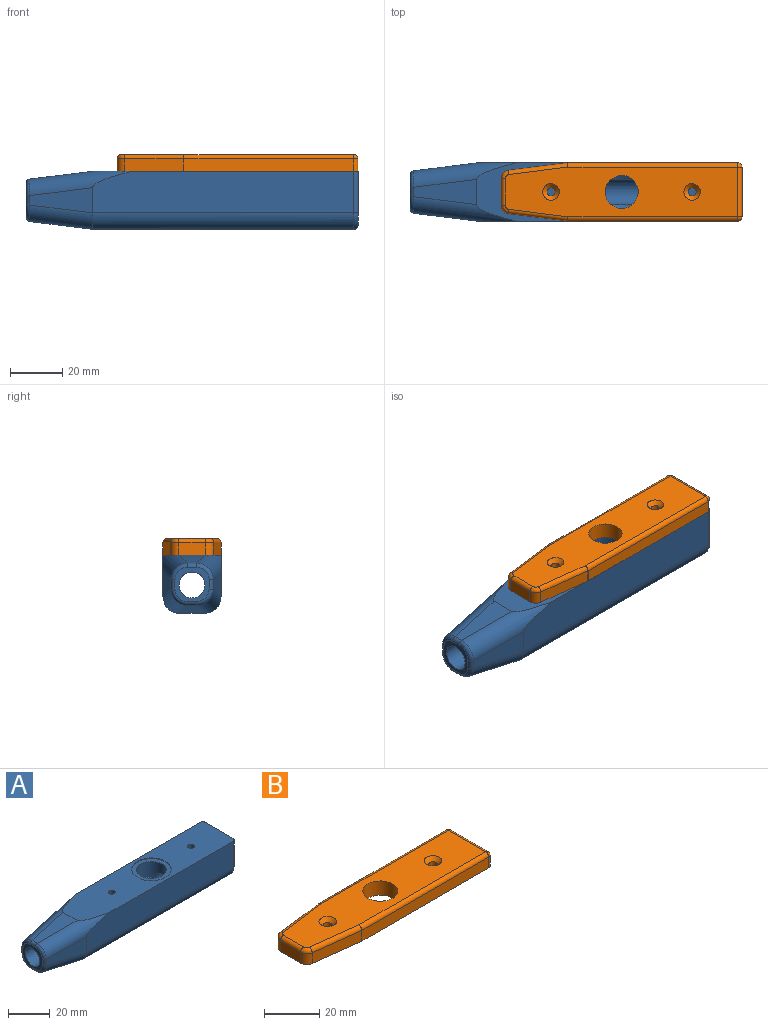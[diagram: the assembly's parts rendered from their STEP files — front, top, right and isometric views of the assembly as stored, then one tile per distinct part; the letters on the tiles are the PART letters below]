
ASSEMBLY  parts=2 mates=1
PART A: 39 faces, bbox 127x26x24.6 mm
  f0: plane 20.62x19.02mm, normal (1,0,0), area 305.2mm2, adj f2,f3,f32,f33,f34,f36,f38
  f1: plane 13.05x13.05mm, normal (-1,0,0), area 73.8mm2, adj f3,f20,f21,f22,f23,f25,f27,f29
  f2: plane 101.51x22.23mm, normal (0,0,1), area 1886mm2, adj f0,f4,f5,f11,f12,f14,f17,f28
  f3: cylinder r=4.97mm len=127mm, axis (1,0,0), area 3790.2mm2, adj f0,f1,f7,f8,f9
  f4: plane 99.91x15.88mm, normal (0,-1,0), area 1552mm2, adj f2,f16,f30,f34,f35
  f5: plane 99.91x15.88mm, normal (0,1,0), area 1552mm2, adj f2,f19,f28,f32,f37
  f6: plane 99.91x9.53mm, normal (0,0,-1), area 951.6mm2, adj f18,f33,f35,f37
  f7: cylinder r=7.15mm len=14.3mm, axis (0,0,1), area 366mm2, adj f3,f8,f9,f10
  f8: cone r=0mm half-angle=59deg, axis (0,0,1), area 19.5mm2, adj f3,f7
  f9: cone r=0mm half-angle=59deg, axis (0,0,1), area 19.5mm2, adj f3,f7
  f10: plane 19.05x19.05mm, normal (0,0,1), area 124.4mm2, adj f7,f11
  f11: cylinder r=9.53mm len=19.05mm, axis (0,0,1), area 24.3mm2, adj f2,f10
  f12: cylinder r=1.59mm len=3.18mm, axis (0,0,1), area 31.7mm2, adj f2,f13
  f13: plane 3.18x3.18mm, normal (0,0,1), area 7.9mm2, adj f12
  f14: cylinder r=1.59mm len=3.18mm, axis (0,0,1), area 31.7mm2, adj f2,f15
  f15: plane 3.18x3.18mm, normal (0,0,1), area 7.9mm2, adj f14
  f16: plane 24.09x9.62mm, normal (-0.12,-0.99,0), area 160.7mm2, adj f4,f20,f26,f30,f35
  f17: plane 24.09x9.62mm, normal (-0.12,0,0.99), area 160.7mm2, adj f2,f21,f28,f30
  f18: plane 24.09x9.62mm, normal (-0.12,0,-0.99), area 160.7mm2, adj f6,f22,f24,f26,f35,f37
  f19: plane 24.09x9.62mm, normal (-0.12,0.99,0), area 160.7mm2, adj f5,f23,f24,f28,f37
  f20: cylinder r=1.6mm len=3.62mm, axis (0,0,-1), area 8.4mm2, adj f1,f16,f27,f31
  f21: cylinder r=1.6mm len=3.62mm, axis (0,-1,0), area 8.4mm2, adj f1,f17,f29,f31
  f22: cylinder r=1.6mm len=3.62mm, axis (0,-1,0), area 8.4mm2, adj f1,f18,f25,f27
  f23: cylinder r=1.6mm len=3.62mm, axis (0,0,-1), area 8.4mm2, adj f1,f19,f25,f29
  f24: cylinder r=6.35mm len=24.4mm, axis (-0.98,-0.12,0.12), area 240mm2, adj f18,f19,f25,f37
  f25: bspline ~6.63x6.63mm, area 20.2mm2, adj f1,f22,f23,f24
  f26: cylinder r=6.35mm len=24.4mm, axis (0.98,-0.12,-0.12), area 240mm2, adj f16,f18,f27,f35
  f27: bspline ~6.3x6.3mm, area 20.2mm2, adj f1,f20,f22,f26
  f28: cylinder r=6.35mm len=39.49mm, axis (-0.98,-0.12,-0.12), area 292.5mm2, adj f2,f5,f17,f19,f29
  f29: bspline ~6.63x6.63mm, area 20.2mm2, adj f1,f21,f23,f28
  f30: cylinder r=6.35mm len=39.49mm, axis (0.98,-0.12,0.12), area 292.5mm2, adj f2,f4,f16,f17,f31
  f31: bspline ~6.3x6.3mm, area 20.2mm2, adj f1,f20,f21,f30
  f32: cylinder r=1.6mm len=15.88mm, axis (0,0,-1), area 39.9mm2, adj f0,f2,f5,f38
  f33: cylinder r=1.6mm len=9.53mm, axis (0,1,0), area 23.9mm2, adj f0,f6,f36,f38
  f34: cylinder r=1.6mm len=15.88mm, axis (0,0,1), area 39.9mm2, adj f0,f2,f4,f36
  f35: cylinder r=6.35mm len=100.07mm, axis (1,0,0), area 997.6mm2, adj f4,f6,f16,f18,f26,f36
  f36: torus R=4.75mm, axis (-1,0,0), area 22.8mm2, adj f0,f33,f34,f35
  f37: cylinder r=6.35mm len=100.07mm, axis (-1,0,0), area 997.6mm2, adj f5,f6,f18,f19,f24,f38
  f38: torus R=4.75mm, axis (-1,0,0), area 22.8mm2, adj f0,f32,f33,f37
PART B: 31 faces, bbox 92.1x22.2x6.4 mm
  f0: plane 64.98x4.75mm, normal (0,-1,0), area 308.6mm2, adj f5,f15,f18,f30
  f1: plane 19.02x4.75mm, normal (1,0,0), area 90.4mm2, adj f5,f16,f18,f20
  f2: plane 64.98x4.75mm, normal (0,1,0), area 308.6mm2, adj f5,f17,f20,f22
  f3: plane 10.27x4.75mm, normal (-1,0,0), area 48.8mm2, adj f5,f13,f14,f26
  f4: plane 88.87x19.02mm, normal (0,0,1), area 1428.6mm2, adj f6,f8,f10,f15,f16,f17,f24,f25
  f5: plane 92.08x22.23mm, normal (0,0,-1), area 1818.9mm2, adj f0,f1,f2,f3,f6,f7,f9,f11
  f6: cylinder r=6.35mm len=12.7mm, axis (0,0,-1), area 253.4mm2, adj f4,f5
  f7: cylinder r=1.59mm len=4.76mm, axis (0,0,1), area 47.5mm2, adj f5,f8
  f8: cone r=1.59mm half-angle=45deg, axis (0,0,1), area 33.6mm2, adj f4,f7
  f9: cylinder r=1.59mm len=4.76mm, axis (0,0,1), area 47.5mm2, adj f5,f10
  f10: cone r=1.59mm half-angle=45deg, axis (0,0,1), area 33.6mm2, adj f4,f9
  f11: plane 22.52x4.75mm, normal (-0.12,-0.99,0), area 107.8mm2, adj f5,f13,f28,f30
  f12: plane 22.52x4.75mm, normal (-0.12,0.99,0), area 107.8mm2, adj f5,f14,f22,f24
  f13: cylinder r=3.17mm len=4.75mm, axis (0,0,-1), area 21.8mm2, adj f3,f5,f11,f27
  f14: cylinder r=3.17mm len=4.75mm, axis (0,0,-1), area 21.8mm2, adj f3,f5,f12,f25
  f15: cylinder r=1.6mm len=64.98mm, axis (-1,0,0), area 163.3mm2, adj f0,f4,f19,f29
  f16: cylinder r=1.6mm len=19.02mm, axis (0,-1,0), area 47.8mm2, adj f1,f4,f19,f21
  f17: cylinder r=1.6mm len=64.98mm, axis (1,0,0), area 163.3mm2, adj f2,f4,f21,f23
  f18: cylinder r=1.6mm len=4.75mm, axis (0,0,1), area 11.9mm2, adj f0,f1,f5,f19
  f19: sphere r=1.6mm, area 4mm2, adj f15,f16,f18
  f20: cylinder r=1.6mm len=4.75mm, axis (0,0,-1), area 11.9mm2, adj f1,f2,f5,f21
  f21: sphere r=1.6mm, area 4mm2, adj f16,f17,f20
  f22: cylinder r=1.6mm len=4.75mm, axis (0,0,-1), area 0.9mm2, adj f2,f5,f12,f23
  f23: sphere r=1.6mm, area 0.3mm2, adj f17,f22,f24
  f24: cylinder r=1.6mm len=22.72mm, axis (-0.99,-0.12,0), area 57mm2, adj f4,f12,f23,f25
  f25: torus R=1.57mm, axis (0,0,1), area 9.4mm2, adj f4,f14,f24,f26
  f26: cylinder r=1.6mm len=10.27mm, axis (0,1,0), area 25.8mm2, adj f3,f4,f25,f27
  f27: torus R=1.57mm, axis (0,0,1), area 9.4mm2, adj f4,f13,f26,f28
  f28: cylinder r=1.6mm len=22.72mm, axis (-0.99,0.12,0), area 57mm2, adj f4,f11,f27,f29
  f29: sphere r=1.6mm, area 0.3mm2, adj f15,f28,f30
  f30: cylinder r=1.6mm len=4.75mm, axis (0,0,1), area 0.9mm2, adj f0,f5,f11,f29
PLACE A t=(-2.86,0.85,-7.36)mm fixed
PLACE B t=(14.59,0.85,14.87)mm
MATE fastened A.f7 <-> B.f6  axis (0,0,1) through (14.59,0.85,14.87)mm
